# Revit family: 0005423 Sylvania Lighting Fixture START Track Spot Integral 930 MB WB BLK
name_source: partatom
category: Lighting Fixtures
revit_build: Autodesk Revit 2017 (Build: 20190507_1515(x64)
units: mm (PartAtom-declared; Revit-internal decimal feet)

## family parameters
Cut with Voids When Loaded = No
Host = Face
Light Source = No
OmniClass Number = 23.80.70.00
OmniClass Title = Lighting
Part Type = Normal
Room Calculation Point = No
Round Connector Dimension = Use Diameter
Shared = No

## types (2) — shared parameters
Apparent Load = 17 VA
Assembly Code = D5020200
AssetType = Fixed
ClassificationName = Uniclass2015
ClassificationValue = EF_70_80
Default Elevation = 1219 mm
DimmingControlOptions = Non dimmable
DocumentationLiterature = http://www.sylvania-lighting.com
DurationUnit = hours
ElectricShockClassification = Class I
ExpectedLife = 50000
IfcExportAs = IfcLightFixtureType
IfcExportType = IfcLightFixtureType
ImpactProtectionIndex = IK03
IngressProtection = IP20
InputNominalFrequency = 50/60 Hz
InputVoltage = 220-240V~
Keynote = 16500
Lamp = LED
LampColourRenderingIndex = 90
LampColourTemperature = 3000
LampMacAdamStep = 3
LampsType = LED
Manufacturer = Feilo Sylvania
ManufacturerName = Feilo Sylvania
Material_1_SYL = Body-Sylvania-StartTrackSpot-Black
Material_2_SYL = Spacer-Sylvania-StartTrackSpot-Aluminium
Material_3_SYL = <By Category>
Material_4_SYL = <By Category>
ModelNumber = 0005423
PowerConsumption = 17 W
Type Image = <None>
TypeArm_SYL = START Track Spot Integral Arm : START Track Spot Integral BL
URL = http://www.sylvania-lighting.com
Voltage = 230 V
Weight = 5.832 kg
zero-valued in all types: Cost, NominalDepth, NominalHeight, NominalLength, PowerFactor

## per-type parameters (varying)
| type | LampNominalLuminous | LuminousEfficacy | Model | ModelReference | Name | TypeHead_SYL | TypeName |
| 0005423 ST TRK SPT INTGRL 1400LM 930 WB BLK | 1400 lm | 96.36 lm/W | START Track Spot Integral 1400lm 930 MB WB BLK | START Track Spot Integral 1400lm 930 MB WB BLK | START Track Spot Integral 1400lm 930 MB WB BLK | START Track Spot Integral Head : 0005423 ST TRK SPT INTGRL 1400LM 930 WB BLK | START Track Spot Integral 1400LM 930 MB WB BLK |
| 0005423 ST TRK SPT INTGRL 1350lm 930 MB BLK | 1350 lm | 90.90 lm/W | START Track Spot Integral 1350lm 930 MB WB BLK | START Track Spot Integral 1350lm 930 MB WB BLK | START Track Spot Integral 1350lm 930 MB WB BLK | START Track Spot Integral Head : 0005423 ST TRK SPT INTGRL 1350LM 930 MB BLK | START Track Spot Integral 1350lm 930 MB WB BLK |

## geometry (parser evidence)
native form markers: Sweep x7
no freeform markers — native parametric forms only
